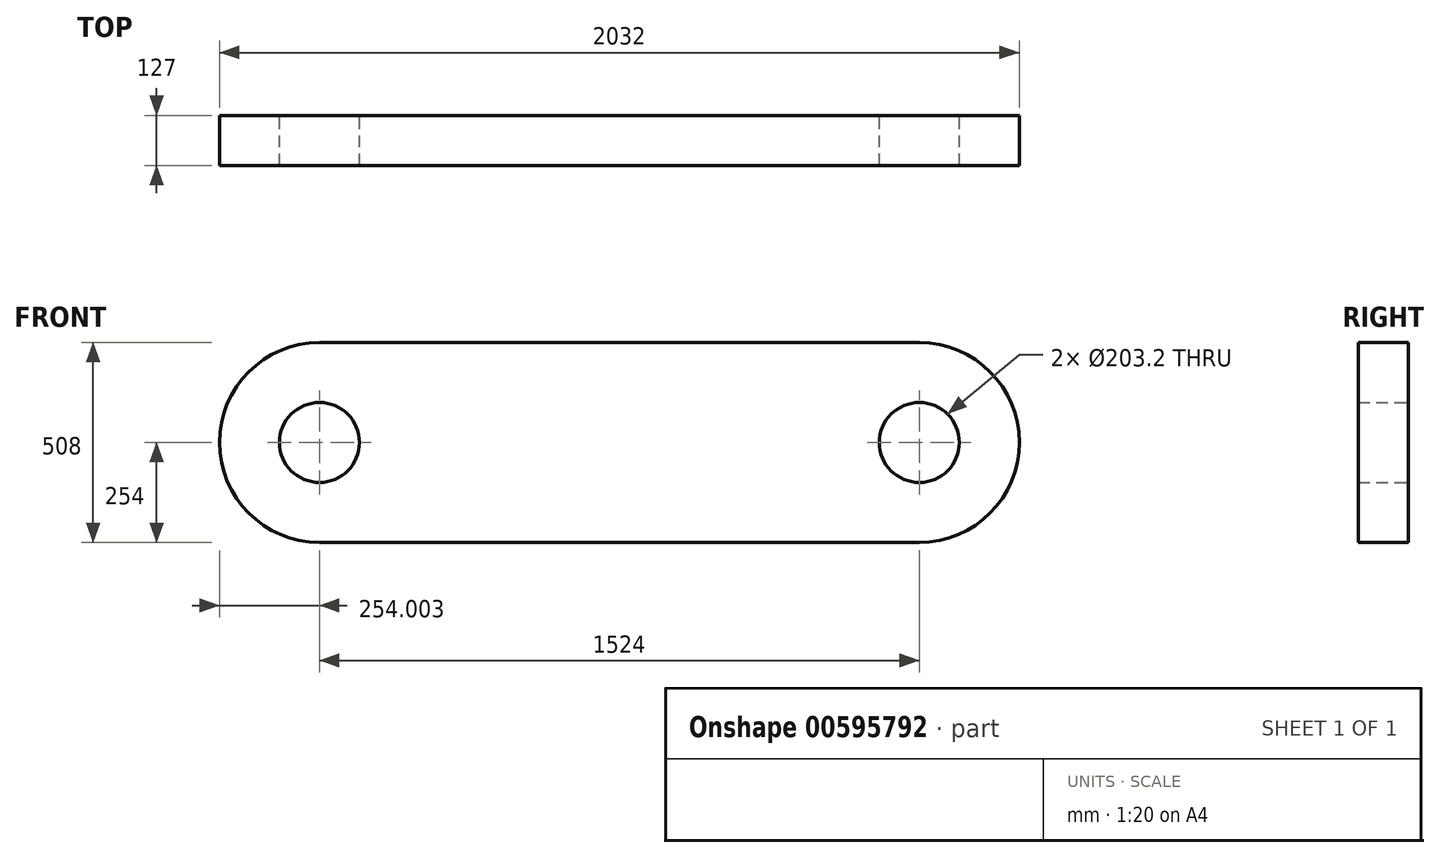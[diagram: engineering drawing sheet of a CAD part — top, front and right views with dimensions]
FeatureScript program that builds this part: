
annotation { "Feature Type Name" : "Feature", "Feature Type Description" : "" }
export const myFeature = defineFeature(function(context is Context, id is Id, definition is map)
    precondition{}
    {
        {
            var Q0;
            Q0=qCreatedBy(makeId("Front.planeOp"),FACE);
            var sketch = newSketch(context, id + "F0", { "sketchPlane" : qUnion([Q0])});
            skLineSegment(sketch, "E0.bottom", {"start": v(-171.39, 415.18) * mm, "end": v(1352.61, 415.18) * mm});
            skLineSegment(sketch, "E0.top", {"start": v(-171.39, -92.82) * mm, "end": v(1352.61, -92.82) * mm});
            skLineSegment(sketch, "E0.left", {"start": v(-171.39, 415.18) * mm, "end": v(-171.39, -92.82) * mm, "construction": true});
            skLineSegment(sketch, "E0.right", {"start": v(1352.61, 415.18) * mm, "end": v(1352.61, -92.82) * mm, "construction": true});
            skArc(sketch, "E1", {"start": v(-171.39, 415.18) * mm, "mid": v(-425.39, 161.18) * mm, "end": v(-171.39, -92.82) * mm});
            skArc(sketch, "E2", {"start": v(1352.61, -92.82) * mm, "mid": v(1606.61, 161.18) * mm, "end": v(1352.61, 415.18) * mm});
            skCircle(sketch, "E3", {"center": v(-171.39, 161.18) * mm, "radius": 101.6 * mm});
            skCircle(sketch, "E4", {"center": v(1352.61, 161.18) * mm, "radius": 101.6 * mm});
            skSolve(sketch);
        }
        {
            var Q0;
            Q0=makeQuery(id+"F0.imprint","IMPRINT",FACE,{"disambiguationData":[TD([[makeQuery(id+"F0.imprint","IMPRINT",EDGE,{"derivedFrom":sQuery(id+"F0.wireOp",EDGE,"E0.bottom")}),-1.0]])]});
            extrude(context, id + "F1", {"entities" : qUnion([Q0]), "depth" : 127 * mm, "offsetDistance" : 25.4 * mm});
        }
    });
